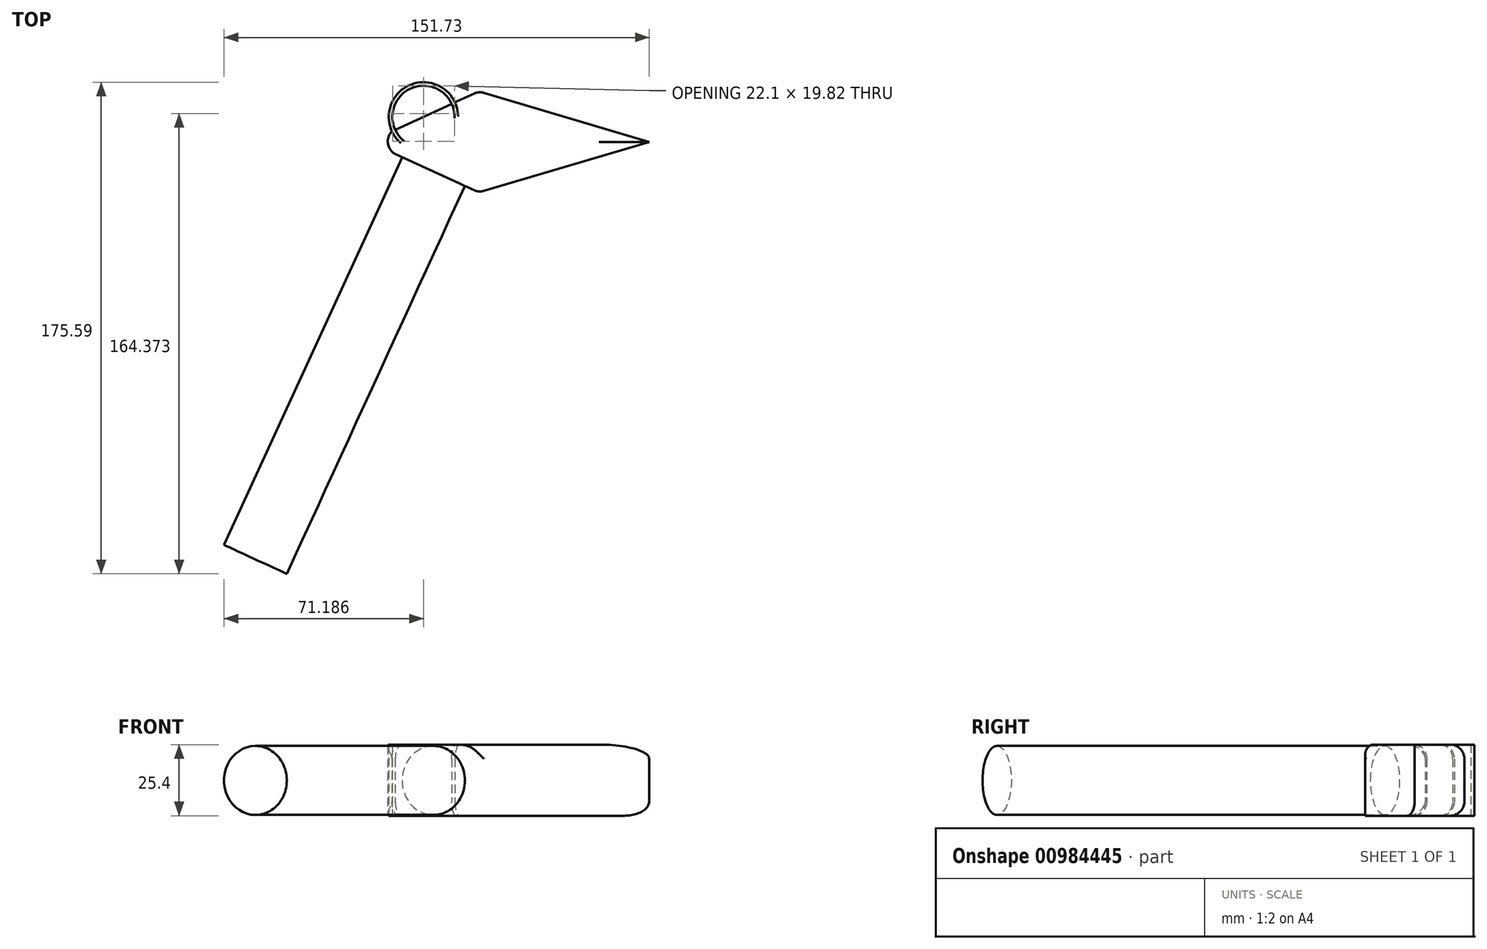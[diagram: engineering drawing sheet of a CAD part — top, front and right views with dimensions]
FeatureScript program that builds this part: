
annotation { "Feature Type Name" : "Feature", "Feature Type Description" : "" }
export const myFeature = defineFeature(function(context is Context, id is Id, definition is map)
    precondition{}
    {
        {
            var Q0;
            Q0=qCreatedBy(makeId("Top.planeOp"),FACE);
            var sketch = newSketch(context, id + "F0", { "sketchPlane" : qUnion([Q0])});
            skLineSegment(sketch, "E0", {"start": v(-39.22, 0) * mm, "end": v(-31, 3.8) * mm});
            skLineSegment(sketch, "E1", {"start": v(0, 18.1) * mm, "end": v(60.79, 0) * mm});
            skLineSegment(sketch, "E2", {"start": v(60.79, 0) * mm, "end": v(0, -17.99) * mm});
            skLineSegment(sketch, "E3", {"start": v(-39.22, 0) * mm, "end": v(0, -17.99) * mm});
            skArc(sketch, "E4", {"start": v(-8.55, 14.16) * mm, "mid": v(-24.96, 20.23) * mm, "end": v(-31, 3.8) * mm});
            skArc(sketch, "E5.0", {"start": v(-9.7, 13.63) * mm, "mid": v(-24.43, 19.08) * mm, "end": v(-29.84, 4.33) * mm});
            skLineSegment(sketch, "E6.trimOffspring", {"start": v(-29.84, 4.33) * mm, "end": v(-9.7, 13.63) * mm});
            skLineSegment(sketch, "E7.trimOffspring", {"start": v(-8.55, 14.16) * mm, "end": v(0, 18.1) * mm});
            skSolve(sketch);
        }
        {
            var Q0;
            {var subQ0=sQuery(id+"F0.wireOp",EDGE,"E1");Q0=makeQuery(id+"F0.imprint","IMPRINT",FACE,{"disambiguationData":[TD([[makeQuery(id+"F0.imprint","IMPRINT",EDGE,{"derivedFrom":subQ0}),-1.0]])]});}
            var Q1;
            {var subQ0=sQuery(id+"F0.wireOp",EDGE,"E4");Q1=makeQuery(id+"F0.imprint","IMPRINT",FACE,{"disambiguationData":[TD([[makeQuery(id+"F0.imprint","IMPRINT",EDGE,{"derivedFrom":subQ0}),1.0]])]});}
            extrude(context, id + "F1", {"entities" : qUnion([Q0, Q1]), "depth" : 25.4 * mm, "offsetDistance" : 25.4 * mm});
        }
        {
            var Q0;
            Q0=makeQuery(id+"F1.opExtrude","CAP_EDGE",EDGE,{"disambiguationData":[OSD([sQuery(id+"F0.wireOp",EDGE,"E7.trimOffspring")])],"isStart":true});
            var Q1;
            Q1=makeQuery(id+"F1.opExtrude","CAP_EDGE",EDGE,{"disambiguationData":[OSD([sQuery(id+"F0.wireOp",EDGE,"E6.trimOffspring")])],"isStart":true});
            var Q2;
            Q2=makeQuery(id+"F1.opExtrude","CAP_EDGE",EDGE,{"disambiguationData":[OSD([sQuery(id+"F0.wireOp",EDGE,"E0")])],"isStart":true});
            var Q3;
            Q3=makeQuery(id+"F1.opExtrude","CAP_EDGE",EDGE,{"disambiguationData":[OSD([sQuery(id+"F0.wireOp",EDGE,"E7.trimOffspring")])],"isStart":false});
            var Q4;
            Q4=makeQuery(id+"F1.opExtrude","CAP_EDGE",EDGE,{"disambiguationData":[OSD([sQuery(id+"F0.wireOp",EDGE,"E6.trimOffspring")])],"isStart":false});
            var Q5;
            Q5=makeQuery(id+"F1.opExtrude","CAP_EDGE",EDGE,{"disambiguationData":[OSD([sQuery(id+"F0.wireOp",EDGE,"E0")])],"isStart":false});
            var Q6;
            Q6=makeQuery(id+"F1.opExtrude","SWEPT_EDGE",EDGE,{"disambiguationData":[OSD([sQuery(id+"F0.wireOp",EDGE,"E0"),sQuery(id+"F0.wireOp",EDGE,"E3")])]});
            var Q7;
            Q7=makeQuery(id+"F1.opExtrude","SWEPT_EDGE",EDGE,{"disambiguationData":[OSD([sQuery(id+"F0.wireOp",EDGE,"E1"),sQuery(id+"F0.wireOp",EDGE,"E7.trimOffspring")])]});
            var Q8;
            Q8=makeQuery(id+"F1.opExtrude","CAP_EDGE",EDGE,{"disambiguationData":[OSD([sQuery(id+"F0.wireOp",EDGE,"E2")])],"isStart":false});
            var Q9;
            Q9=makeQuery(id+"F1.opExtrude","CAP_EDGE",EDGE,{"disambiguationData":[OSD([sQuery(id+"F0.wireOp",EDGE,"E1")])],"isStart":true});
            var Q10;
            Q10=makeQuery(id+"F1.opExtrude","CAP_EDGE",EDGE,{"disambiguationData":[OSD([sQuery(id+"F0.wireOp",EDGE,"E1")])],"isStart":false});
            var Q11;
            Q11=makeQuery(id+"F1.opExtrude","SWEPT_EDGE",EDGE,{"disambiguationData":[OSD([sQuery(id+"F0.wireOp",EDGE,"E2"),sQuery(id+"F0.wireOp",EDGE,"E3")])]});
            fillet(context, id + "F2", {"entities" : qUnion([Q0, Q1, Q2, Q3, Q4, Q5, Q6, Q7, Q8, Q9, Q10, Q11]), "radius" : 5.08 * mm, "tangentPropagation" : true, "allowEdgeOverflow" : false});
        }
        {
            var Q0;
            Q0=makeQuery(id+"F1.opExtrude","SWEPT_FACE",FACE,{"disambiguationData":[OSD([sQuery(id+"F0.wireOp",EDGE,"E3")])]});
            var sketch = newSketch(context, id + "F3", { "sketchPlane" : qUnion([Q0])});
            skCircle(sketch, "E8", {"center": v(-10.33, 12.6) * mm, "radius": 12.32 * mm});
            skSolve(sketch);
        }
        {
            var Q0;
            Q0=makeQuery(id+"F3.imprint","IMPRINT",FACE,{"disambiguationData":[TD([[makeQuery(id+"F3.imprint","IMPRINT",EDGE,{"derivedFrom":sQuery(id+"F3.wireOp",EDGE,"E8")}),1.0]])]});
            extrude(context, id + "F4", {"entities" : qUnion([Q0]), "operationType" : NewBodyOperationType.ADD, "depth" : 152.4 * mm, "offsetDistance" : 25.4 * mm});
        }
        {
            var Q0;
            Q0=makeQuery(id+"F4.opExtrude","CAP_FACE",FACE,{"disambiguationData":[OSD([sQuery(id+"F3.wireOp",EDGE,"E8")])],"isStart":false});
            var sketch = newSketch(context, id + "F5", { "sketchPlane" : qUnion([Q0])});
            skLineSegment(sketch, "E9.bottom", {"start": v(-83.26, 128.8) * mm, "end": v(70.77, 128.8) * mm});
            skLineSegment(sketch, "E9.top", {"start": v(-83.26, -102.16) * mm, "end": v(70.77, -102.16) * mm});
            skLineSegment(sketch, "E9.left", {"start": v(-83.26, 128.8) * mm, "end": v(-83.26, -102.16) * mm});
            skLineSegment(sketch, "E9.right", {"start": v(70.77, 128.8) * mm, "end": v(70.77, -102.16) * mm});
            skSolve(sketch);
        }
        {
            var Q0;
            Q0 = qSketchRegion(id + "F5", true);
            extrude(context, id + "F6", {"entities" : qUnion([Q0]), "operationType" : NewBodyOperationType.ADD, "oppositeDirection" : true, "depth" : 43.18 * mm, "offsetDistance" : 25.4 * mm});
        }
        {
            var Q0;
            Q0=makeQuery(id+"F6.opExtrude","SWEPT_FACE",FACE,{"disambiguationData":[OSD([sQuery(id+"F5.wireOp",EDGE,"E9.left")])]});
            var sketch = newSketch(context, id + "F7", { "sketchPlane" : qUnion([Q0])});
            skLineSegment(sketch, "E10", {"start": v(168.75, 112.27) * mm, "end": v(131.08, 112.27) * mm});
            skLineSegment(sketch, "E11", {"start": v(131.08, 112.27) * mm, "end": v(131.08, -86.33) * mm});
            skLineSegment(sketch, "E12", {"start": v(168.75, -86.32) * mm, "end": v(131.08, -86.32) * mm});
            skSolve(sketch);
        }
        {
            var Q0;
            Q0=makeQuery(id+"F6.opExtrude","CAP_FACE",FACE,{"disambiguationData":[OSD([sQuery(id+"F5.wireOp",EDGE,"E9.bottom"),sQuery(id+"F5.wireOp",EDGE,"E9.top"),sQuery(id+"F5.wireOp",EDGE,"E9.left"),sQuery(id+"F5.wireOp",EDGE,"E9.right")])],"isStart":false});
            var Q1;
            Q1=makeQuery(id+"F6.boolean.opBoolean","MERGE",FACE,{"derivedFrom":[makeQuery(id+"F4.opExtrude","CAP_FACE",FACE,{"disambiguationData":[OSD([sQuery(id+"F3.wireOp",EDGE,"E8")])],"isStart":false}),makeQuery(id+"F6.opExtrude","CAP_FACE",FACE,{"disambiguationData":[OSD([sQuery(id+"F5.wireOp",EDGE,"E9.bottom"),sQuery(id+"F5.wireOp",EDGE,"E9.top"),sQuery(id+"F5.wireOp",EDGE,"E9.left"),sQuery(id+"F5.wireOp",EDGE,"E9.right")])],"isStart":true})]});
            var Q2;
            {var subQ0=sQuery(id+"F7.wireOp",EDGE,"E10");Q2=makeQuery(id+"F7.imprint","IMPRINT",FACE,{"disambiguationData":[TD([[makeQuery(id+"F7.imprint","IMPRINT",EDGE,{"derivedFrom":subQ0}),1.0]])]});}
            extrude(context, id + "F8", {"entities" : qUnion([Q0, Q1, Q2]), "operationType" : NewBodyOperationType.REMOVE, "endBound" : BoundingType.THROUGH_ALL, "oppositeDirection" : true, "depth" : 25.4 * mm, "offsetDistance" : 25.4 * mm});
        }
    });
